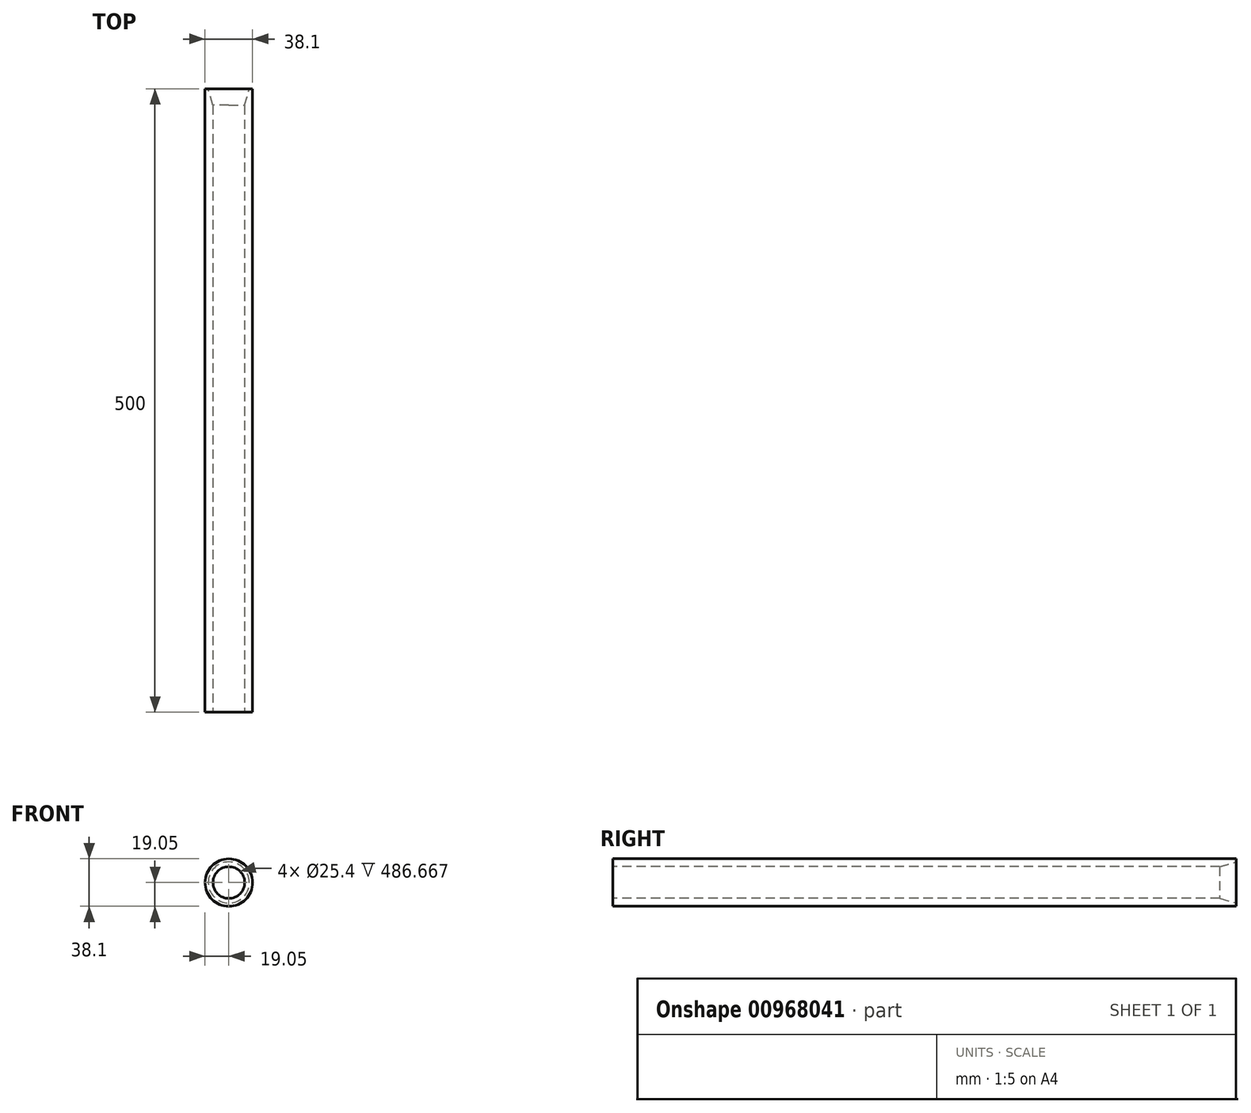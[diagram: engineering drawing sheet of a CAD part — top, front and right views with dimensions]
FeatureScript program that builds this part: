
annotation { "Feature Type Name" : "Feature", "Feature Type Description" : "" }
export const myFeature = defineFeature(function(context is Context, id is Id, definition is map)
    precondition{}
    {
        {
            var Q0;
            Q0=qCreatedBy(makeId("Right.planeOp"),FACE);
            var sketch = newSketch(context, id + "F0", { "sketchPlane" : qUnion([Q0])});
            skLineSegment(sketch, "E0", {"start": v(0, 0) * mm, "end": v(0, 19.05) * mm});
            skLineSegment(sketch, "E1", {"start": v(0, 19.05) * mm, "end": v(500, 19.05) * mm});
            skLineSegment(sketch, "E2", {"start": v(500, 19.05) * mm, "end": v(500, 16.51) * mm});
            skLineSegment(sketch, "E3", {"start": v(460, 5.08) * mm, "end": v(500, 16.51) * mm});
            skLineSegment(sketch, "E4", {"start": v(0, 0) * mm, "end": v(460, 0) * mm});
            skLineSegment(sketch, "E5", {"start": v(460, 5.08) * mm, "end": v(460, 0) * mm});
            skSolve(sketch);
        }
        {
            var Q0;
            Q0=qCreatedBy(makeId("Front.planeOp"),FACE);
            var sketch = newSketch(context, id + "F1", { "sketchPlane" : qUnion([Q0])});
            skCircle(sketch, "E6", {"center": v(0, 0) * mm, "radius": 19.05 * mm});
            skSolve(sketch);
        }
        {
            var Q0;
            Q0=makeQuery(id+"F0.imprint","IMPRINT",FACE,{"disambiguationData":[TD([[makeQuery(id+"F0.imprint","IMPRINT",EDGE,{"derivedFrom":sQuery(id+"F0.wireOp",EDGE,"E0")}),-1.0]])]});
            var Q1;
            Q1=sQuery(id+"F1.wireOp",EDGE,"E6");
            revolve(context, id + "F2", {"surfaceOperationType" : NewSurfaceOperationType.NEW, "entities" : qUnion([Q0]), "axis" : qUnion([Q1]), "revolveType" : RevolveType.FULL});
        }
        {
            var Q0;
            Q0=qCreatedBy(makeId("Front.planeOp"),FACE);
            var sketch = newSketch(context, id + "F3", { "sketchPlane" : qUnion([Q0])});
            skCircle(sketch, "E7", {"center": v(0, 0) * mm, "radius": 12.7 * mm});
            skSolve(sketch);
        }
        {
            var Q0;
            Q0=makeQuery(id+"F3.imprint","IMPRINT",FACE,{"disambiguationData":[TD([[makeQuery(id+"F3.imprint","IMPRINT",EDGE,{"derivedFrom":sQuery(id+"F3.wireOp",EDGE,"E7")}),1.0]])]});
            extrude(context, id + "F4", {"entities" : qUnion([Q0]), "operationType" : NewBodyOperationType.REMOVE, "endBound" : BoundingType.THROUGH_ALL, "oppositeDirection" : true, "depth" : 25 * mm, "offsetDistance" : 25 * mm});
        }
    });
